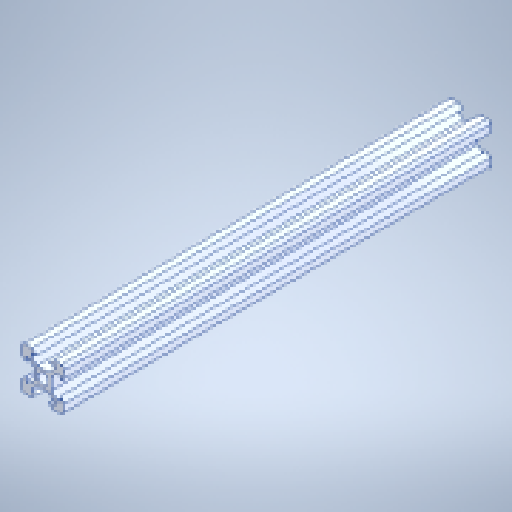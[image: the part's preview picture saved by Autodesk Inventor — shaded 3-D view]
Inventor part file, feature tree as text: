
AUTODESK INVENTOR PART (.ipt)
format: ipt  version: 2025.1 (Build 291241020, 241B)  size: 285,184 bytes
history: native  units: in
note: dims shown in document units (in); Inventor stores cm internally (conversion verified against a paired STEP export)
features: extrude x2, sketch x1, projected_geometry x1, other x1
ambient origin geometry x8: Origin, YZ Plane, XZ Plane, XY Plane, X Axis, Y Axis, Z Axis, Center Point
bodies: Solid1 (feature_tree)
feature tree (5):
  sketch  "Sketch1"  dims[d0=7.874in d1=0.0in d2=5.9055in d3=0.0in]
  extrude  "Extrusion1"  Depth=5.9055in TaperAngle=0.0deg
  extrude  "Extrusion2"  [1 undecoded]
  projected_geometry  "Projected Loop1"
  other  "Скругление1"
note: 1 required parameter value undecoded (feature->parameter linkage not recoverable at this tier; creation-order binding heuristic only, values carry confidence <= 0.55)
